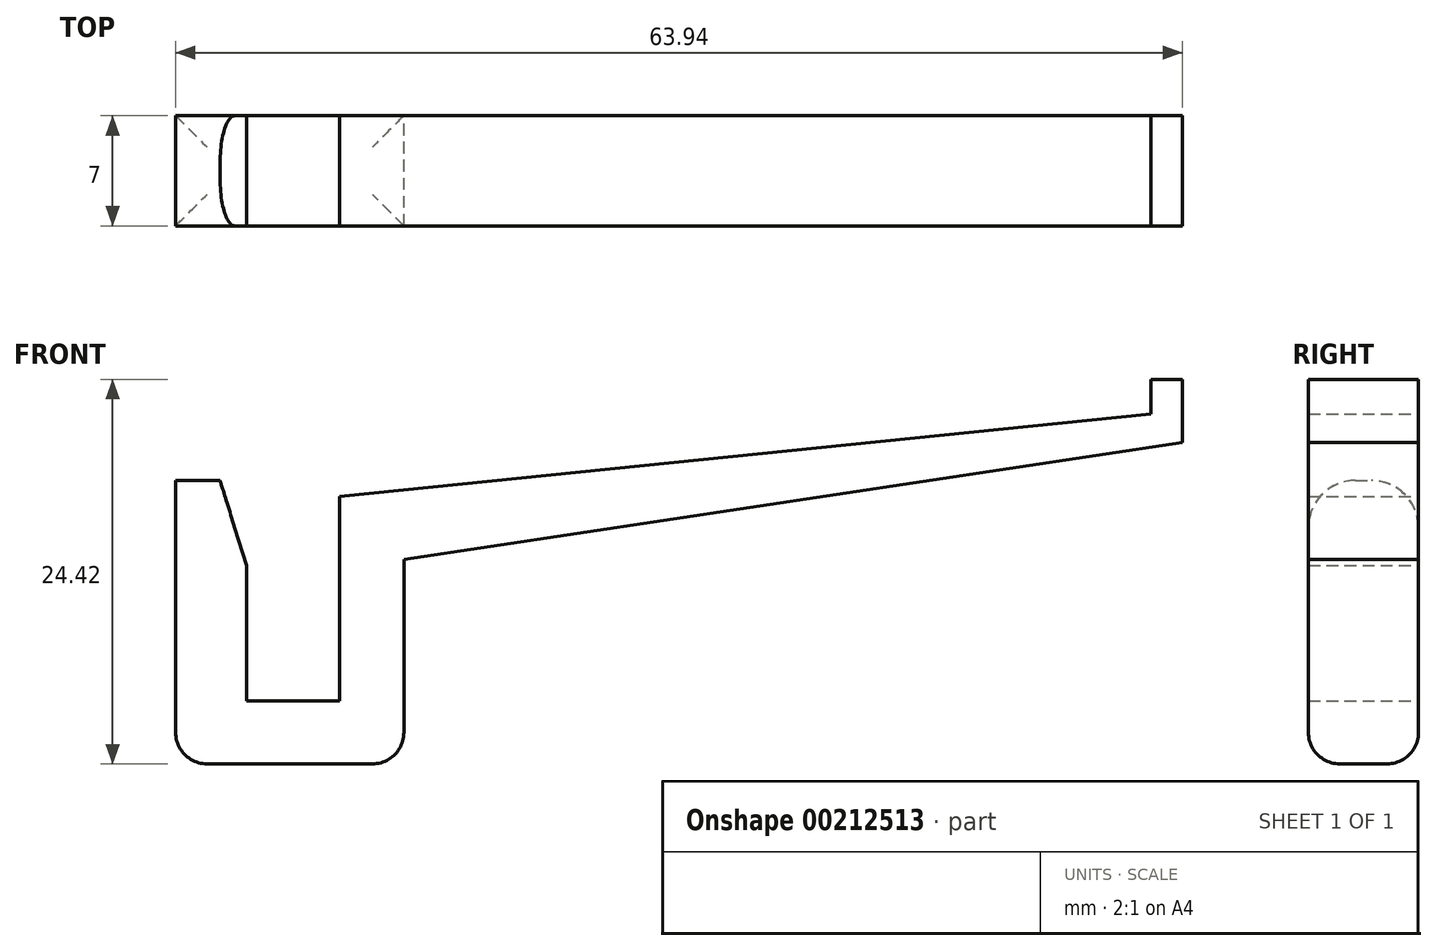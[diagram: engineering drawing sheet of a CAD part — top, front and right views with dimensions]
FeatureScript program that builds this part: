
annotation { "Feature Type Name" : "Feature", "Feature Type Description" : "" }
export const myFeature = defineFeature(function(context is Context, id is Id, definition is map)
    precondition{}
    {
        {
            var Q0;
            Q0=qCreatedBy(makeId("Front.planeOp"),FACE);
            var sketch = newSketch(context, id + "F0", { "sketchPlane" : qUnion([Q0])});
            skLineSegment(sketch, "E0", {"start": v(-11.91, -8.61) * mm, "end": v(-11.91, 0) * mm});
            skLineSegment(sketch, "E1", {"start": v(-16.41, 0.39) * mm, "end": v(-16.41, -12.61) * mm});
            skLineSegment(sketch, "E2", {"start": v(-16.41, -12.61) * mm, "end": v(-1.91, -12.61) * mm});
            skLineSegment(sketch, "E3", {"start": v(-1.91, -12.61) * mm, "end": v(-1.91, -3.61) * mm});
            skLineSegment(sketch, "E4", {"start": v(-6.01, 0.39) * mm, "end": v(-6.01, -8.61) * mm});
            skLineSegment(sketch, "E5", {"start": v(-6.01, -8.61) * mm, "end": v(-11.91, -8.61) * mm});
            skLineSegment(sketch, "E6", {"start": v(-15.26, 5.39) * mm, "end": v(-13.59, 5.39) * mm});
            skLineSegment(sketch, "E7", {"start": v(-16.41, 0.39) * mm, "end": v(-16.41, 5.39) * mm});
            skLineSegment(sketch, "E8", {"start": v(-15.26, 5.39) * mm, "end": v(-16.41, 5.39) * mm});
            skLineSegment(sketch, "E9", {"start": v(-6.01, 0.39) * mm, "end": v(-6.01, 4.39) * mm});
            skLineSegment(sketch, "E10", {"start": v(-6.01, 4.39) * mm, "end": v(45.53, 9.6) * mm});
            skLineSegment(sketch, "E11", {"start": v(47.53, 9.8) * mm, "end": v(47.53, 7.8) * mm});
            skLineSegment(sketch, "E12", {"start": v(-1.91, -3.61) * mm, "end": v(-1.91, 0.39) * mm});
            skLineSegment(sketch, "E13", {"start": v(47.53, 7.8) * mm, "end": v(-1.91, 0.39) * mm});
            skLineSegment(sketch, "E14", {"start": v(47.53, 9.8) * mm, "end": v(47.53, 11.8) * mm});
            skLineSegment(sketch, "E15", {"start": v(47.53, 11.8) * mm, "end": v(45.53, 11.8) * mm});
            skLineSegment(sketch, "E16", {"start": v(45.53, 11.8) * mm, "end": v(45.53, 9.6) * mm});
            skLineSegment(sketch, "E17", {"start": v(-13.59, 5.39) * mm, "end": v(-11.91, 0) * mm});
            skPoint(sketch, "E18.orphan", {"position": v(-11.91, 5.39) * mm});
            skSolve(sketch);
        }
        {
            var Q0;
            Q0=makeQuery(id+"F0.imprint","IMPRINT",FACE,{"disambiguationData":[TD([[makeQuery(id+"F0.imprint","IMPRINT",EDGE,{"derivedFrom":sQuery(id+"F0.wireOp",EDGE,"E0")}),1.0]])]});
            extrude(context, id + "F1", {"entities" : qUnion([Q0]), "endBound" : BoundingType.SYMMETRIC, "depth" : 7 * mm});
        }
        {
            var Q0;
            Q0=makeQuery(id+"F1.opExtrude","CAP_EDGE",EDGE,{"disambiguationData":[OSD([sQuery(id+"F0.wireOp",EDGE,"E6"),sQuery(id+"F0.wireOp",EDGE,"E8")])],"isStart":false});
            var Q1;
            Q1=makeQuery(id+"F1.opExtrude","CAP_EDGE",EDGE,{"disambiguationData":[OSD([sQuery(id+"F0.wireOp",EDGE,"E6"),sQuery(id+"F0.wireOp",EDGE,"E8")])],"isStart":true});
            fillet(context, id + "F2", {"entities" : qUnion([Q0, Q1]), "radius" : 3 * mm, "tangentPropagation" : true, "allowEdgeOverflow" : false});
        }
        {
            var Q0;
            Q0=makeQuery(id+"F1.opExtrude","SWEPT_FACE",FACE,{"disambiguationData":[OSD([sQuery(id+"F0.wireOp",EDGE,"E2")])]});
            fillet(context, id + "F3", {"entities" : qUnion([Q0]), "radius" : 2 * mm, "tangentPropagation" : true, "allowEdgeOverflow" : false});
        }
    });
